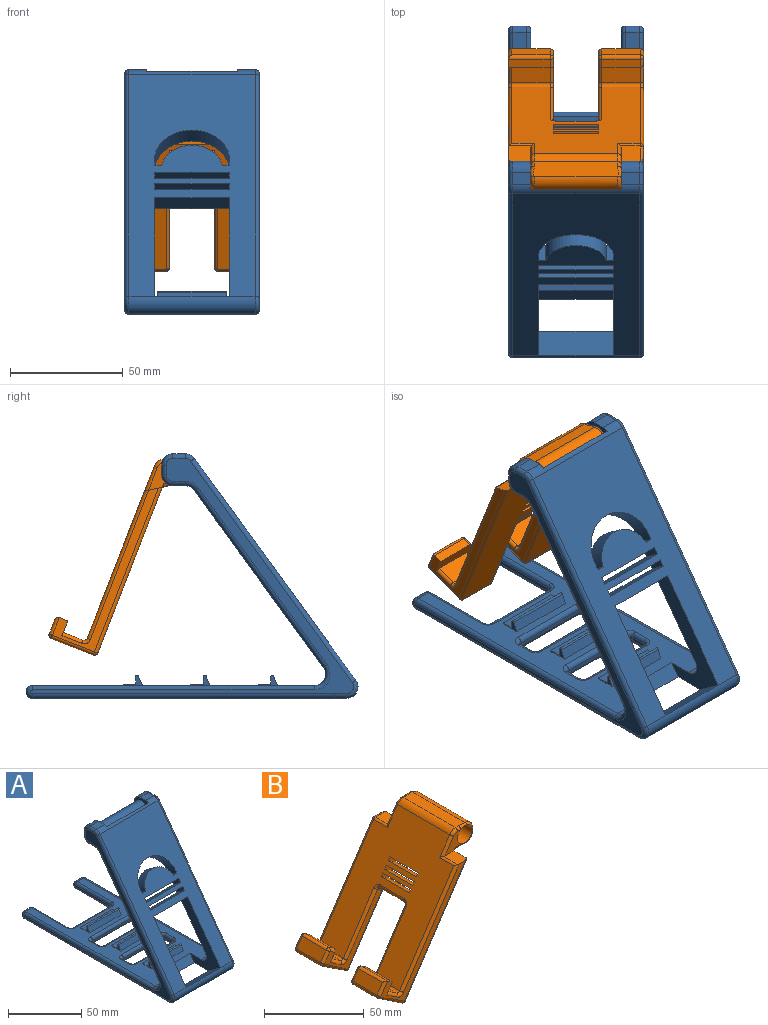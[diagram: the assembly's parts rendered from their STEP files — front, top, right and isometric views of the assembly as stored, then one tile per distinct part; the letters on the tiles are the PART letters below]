
ASSEMBLY  parts=2 mates=1
PART A: 162 faces, bbox 60x147.8x109.3 mm
  f0: plane 80.74x58.78mm, normal (0,0.81,-0.59), area 3689.6mm2, adj f2,f15,f18,f19,f20,f24,f26,f66
  f1: plane 98.49x71.71mm, normal (0,-0.81,0.59), area 4530.3mm2, adj f12,f23,f71,f130,f147,f148,f149,f150
  f2: cylinder r=5mm len=11.5mm, axis (-1,0,0), area 126.5mm2, adj f0,f3,f68,f148
  f3: plane 125.18x56mm, normal (0,0,1), area 2944.3mm2, adj f2,f5,f14,f15,f29,f33,f34,f35
  f4: plane 134.3x56mm, normal (0,0,-1), area 4121.6mm2, adj f5,f13,f14,f74,f81,f86,f87,f90
  f5: cylinder r=2.83mm len=6mm, axis (-1,0,0), area 53.3mm2, adj f3,f4,f122,f137
  f6: plane 8x4.2mm, normal (0,1,0), area 33.6mm2, adj f18,f22,f25,f138
  f7: plane 8x5.5mm, normal (0,0,1), area 44mm2, adj f18,f22,f23,f134
  f8: plane 8x5.5mm, normal (0,0,-1), area 44mm2, adj f20,f26,f27,f62
  f9: plane 8x5.5mm, normal (0,0,-1), area 44mm2, adj f18,f24,f25,f142
  f10: plane 8x4.2mm, normal (0,1,0), area 33.6mm2, adj f20,f27,f28,f63
  f11: plane 8x5.5mm, normal (0,0,1), area 44mm2, adj f20,f23,f28,f67
  f12: cylinder r=5mm len=56mm, axis (-1,0,0), area 613.6mm2, adj f1,f13,f73,f131,f145
  f13: plane 56x5.34mm, normal (0,-0.01,-1), area 299.3mm2, adj f4,f12,f75,f133
  f14: cylinder r=2.83mm len=6mm, axis (-1,0,0), area 53.3mm2, adj f3,f4,f72,f119
  f15: cylinder r=5mm len=11.5mm, axis (-1,0,0), area 126.5mm2, adj f0,f3,f141,f147
  f16: plane 143.43x104.54mm, normal (1,0,0), area 912.6mm2, adj f61,f62,f63,f64,f65,f66,f67,f68
  f17: plane 143.43x104.54mm, normal (-1,0,0), area 912.6mm2, adj f130,f131,f132,f133,f134,f135,f136,f137
  f18: plane 16.26x14.54mm, normal (1,0,0), area 96.4mm2, adj f0,f6,f7,f9,f19,f21,f22,f23
  f19: plane 40x13.51mm, normal (0,1,0), area 540.2mm2, adj f0,f18,f20,f23
  f20: plane 16.26x14.54mm, normal (-1,0,0), area 96.4mm2, adj f0,f8,f10,f11,f19,f21,f23,f26
  f21: cylinder r=5mm len=40mm, axis (-1,0,0), area 1256.6mm2, adj f18,f20
  f22: cylinder r=5mm len=8mm, axis (-1,0,0), area 62.8mm2, adj f6,f7,f18,f136
  f23: cylinder r=5mm len=56mm, axis (1,0,0), area 156.8mm2, adj f1,f7,f11,f18,f19,f20,f69,f132
  f24: cylinder r=5mm len=8mm, axis (-1,0,0), area 37.7mm2, adj f0,f9,f18,f144
  f25: cylinder r=5mm len=8mm, axis (-1,0,0), area 62.8mm2, adj f6,f9,f18,f140
  f26: cylinder r=5mm len=8mm, axis (-1,0,0), area 37.7mm2, adj f0,f8,f20,f64
  f27: cylinder r=5mm len=8mm, axis (-1,0,0), area 62.8mm2, adj f8,f10,f20,f61
  f28: cylinder r=5mm len=8mm, axis (-1,0,0), area 62.8mm2, adj f10,f11,f20,f65
  f29: plane 30.6x0.56mm, normal (0,1,0), area 17mm2, adj f3,f30,f34,f35
  f30: plane 30.6x5.48mm, normal (0,0,1), area 167.7mm2, adj f29,f31,f34,f35
  f31: plane 30.6x3.41mm, normal (0,1,0), area 104.3mm2, adj f30,f32,f34,f35
  f32: cylinder r=0.62mm len=30.6mm, axis (1,0,0), area 54.6mm2, adj f31,f33,f34,f35
  f33: plane 30.6x4.14mm, normal (0,-0.92,0.39), area 137.7mm2, adj f3,f32,f34,f35
  f34: plane 8.47x4.59mm, normal (-1,0,0), area 12.2mm2, adj f3,f29,f30,f31,f32,f33
  f35: plane 8.47x4.59mm, normal (1,0,0), area 12.2mm2, adj f3,f29,f30,f31,f32,f33
  f36: plane 30.6x0.56mm, normal (0,1,0), area 17mm2, adj f3,f37,f41,f42
  f37: plane 30.6x5.48mm, normal (0,0,1), area 167.7mm2, adj f36,f38,f41,f42
  f38: plane 30.6x3.41mm, normal (0,1,0), area 104.3mm2, adj f37,f39,f41,f42
  f39: cylinder r=0.62mm len=30.6mm, axis (1,0,0), area 54.6mm2, adj f38,f40,f41,f42
  f40: plane 30.6x4.14mm, normal (0,-0.92,0.39), area 137.7mm2, adj f3,f39,f41,f42
  f41: plane 8.47x4.59mm, normal (-1,0,0), area 12.2mm2, adj f3,f36,f37,f38,f39,f40
  f42: plane 8.47x4.59mm, normal (1,0,0), area 12.2mm2, adj f3,f36,f37,f38,f39,f40
  f43: plane 30.6x0.56mm, normal (0,1,0), area 17mm2, adj f3,f44,f48,f49
  f44: plane 30.6x5.48mm, normal (0,0,1), area 167.7mm2, adj f43,f45,f48,f49
  f45: plane 30.6x3.41mm, normal (0,1,0), area 104.3mm2, adj f44,f46,f48,f49
  f46: cylinder r=0.62mm len=30.6mm, axis (1,0,0), area 54.6mm2, adj f45,f47,f48,f49
  f47: plane 30.6x4.14mm, normal (0,-0.92,0.39), area 137.7mm2, adj f3,f46,f48,f49
  f48: plane 8.47x4.59mm, normal (-1,0,0), area 12.2mm2, adj f3,f43,f44,f45,f46,f47
  f49: plane 8.47x4.59mm, normal (1,0,0), area 12.2mm2, adj f3,f43,f44,f45,f46,f47
  f50: plane 36x1.65mm, normal (0,1,0), area 59.6mm2, adj f117,f124,f125,f129
  f51: plane 34.26x1.65mm, normal (-1,0,0), area 56.4mm2, adj f116,f119,f123,f124
  f52: plane 34.26x1.65mm, normal (1,0,0), area 56.4mm2, adj f118,f122,f125,f126
  f53: plane 36x1.65mm, normal (0,1,0), area 59.6mm2, adj f99,f100,f109,f110
  f54: plane 7x1.65mm, normal (-1,0,0), area 11.6mm2, adj f104,f109,f112,f115
  f55: plane 36x1.65mm, normal (0,-1,0), area 59.6mm2, adj f102,f103,f111,f112
  f56: plane 7x1.65mm, normal (1,0,0), area 11.6mm2, adj f96,f100,f101,f102
  f57: plane 36x1.65mm, normal (0,1,0), area 59.6mm2, adj f79,f80,f89,f90
  f58: plane 7x1.65mm, normal (-1,0,0), area 11.6mm2, adj f84,f89,f92,f95
  f59: plane 36x1.65mm, normal (0,-1,0), area 59.6mm2, adj f82,f83,f91,f92
  f60: plane 7x1.65mm, normal (1,0,0), area 11.6mm2, adj f76,f80,f81,f82
  f61: torus R=3mm, axis (1,0,0), area 21.1mm2, adj f16,f27,f62,f63
  f62: cylinder r=2mm len=5.5mm, axis (0,-1,0), area 17.3mm2, adj f8,f16,f61,f64
  f63: cylinder r=2mm len=4.2mm, axis (0,0,-1), area 13.2mm2, adj f10,f16,f61,f65
  f64: torus R=7mm, axis (1,0,0), area 16.9mm2, adj f16,f26,f62,f66
  f65: torus R=3mm, axis (1,0,0), area 21.1mm2, adj f16,f28,f63,f67
  f66: cylinder r=2mm len=79.86mm, axis (0,-0.59,-0.81), area 305.8mm2, adj f0,f16,f64,f68
  f67: cylinder r=2mm len=5.5mm, axis (0,1,0), area 17.3mm2, adj f11,f16,f65,f69
  f68: torus R=7mm, axis (1,0,0), area 39.6mm2, adj f2,f16,f66,f70
  f69: torus R=3mm, axis (1,0,0), area 12.6mm2, adj f16,f23,f67,f71
  f70: cylinder r=2mm len=125.18mm, axis (0,1,0), area 393.3mm2, adj f3,f16,f68,f72
  f71: cylinder r=2mm len=99.67mm, axis (0,0.59,0.81), area 382.7mm2, adj f1,f16,f69,f73
  f72: torus R=0.83mm, axis (1,0,0), area 20.7mm2, adj f14,f16,f70,f74
  f73: torus R=3mm, axis (1,0,0), area 29.4mm2, adj f12,f16,f71,f75
  f74: cylinder r=2mm len=134.3mm, axis (0,-1,0), area 421.9mm2, adj f4,f16,f72,f75
  f75: cylinder r=2mm len=5.36mm, axis (0,-1,0.01), area 16.8mm2, adj f13,f16,f73,f74
  f76: cylinder r=2mm len=7mm, axis (0,1,0), area 22mm2, adj f3,f60,f77,f78
  f77: torus R=4mm, axis (0,0,1), area 13.5mm2, adj f3,f76,f79,f80
  f78: torus R=4mm, axis (0,0,1), area 13.5mm2, adj f3,f76,f82,f83
  f79: cylinder r=2mm len=36mm, axis (-1,0,0), area 113.1mm2, adj f3,f57,f77,f85
  f80: cylinder r=2mm len=2mm, axis (0,0,-1), area 5.2mm2, adj f57,f60,f77,f86
  f81: cylinder r=2mm len=7mm, axis (0,-1,0), area 22mm2, adj f4,f60,f86,f87
  f82: cylinder r=2mm len=2mm, axis (0,0,1), area 5.2mm2, adj f59,f60,f78,f87
  f83: cylinder r=2mm len=36mm, axis (1,0,0), area 113.1mm2, adj f3,f59,f78,f88
  f84: cylinder r=2mm len=7mm, axis (0,-1,0), area 22mm2, adj f3,f58,f85,f88
  f85: torus R=4mm, axis (0,0,1), area 13.5mm2, adj f3,f79,f84,f89
  f86: torus R=4mm, axis (0,0,1), area 13.5mm2, adj f4,f80,f81,f90
  f87: torus R=4mm, axis (0,0,1), area 13.5mm2, adj f4,f81,f82,f91
  f88: torus R=4mm, axis (0,0,1), area 13.5mm2, adj f3,f83,f84,f92
  f89: cylinder r=2mm len=2mm, axis (0,0,1), area 5.2mm2, adj f57,f58,f85,f93
  f90: cylinder r=2mm len=36mm, axis (1,0,0), area 113.1mm2, adj f4,f57,f86,f93
  f91: cylinder r=2mm len=36mm, axis (-1,0,0), area 113.1mm2, adj f4,f59,f87,f94
  f92: cylinder r=2mm len=2mm, axis (0,0,-1), area 5.2mm2, adj f58,f59,f88,f94
  f93: torus R=4mm, axis (0,0,1), area 13.5mm2, adj f4,f89,f90,f95
  f94: torus R=4mm, axis (0,0,1), area 13.5mm2, adj f4,f91,f92,f95
  f95: cylinder r=2mm len=7mm, axis (0,1,0), area 22mm2, adj f4,f58,f93,f94
  f96: cylinder r=2mm len=7mm, axis (0,1,0), area 22mm2, adj f3,f56,f97,f98
  f97: torus R=4mm, axis (0,0,1), area 13.5mm2, adj f3,f96,f99,f100
  f98: torus R=4mm, axis (0,0,1), area 13.5mm2, adj f3,f96,f102,f103
  f99: cylinder r=2mm len=36mm, axis (-1,0,0), area 113.1mm2, adj f3,f53,f97,f105
  f100: cylinder r=2mm len=2mm, axis (0,0,-1), area 5.2mm2, adj f53,f56,f97,f106
  f101: cylinder r=2mm len=7mm, axis (0,-1,0), area 22mm2, adj f4,f56,f106,f107
  f102: cylinder r=2mm len=2mm, axis (0,0,1), area 5.2mm2, adj f55,f56,f98,f107
  f103: cylinder r=2mm len=36mm, axis (1,0,0), area 113.1mm2, adj f3,f55,f98,f108
  f104: cylinder r=2mm len=7mm, axis (0,-1,0), area 22mm2, adj f3,f54,f105,f108
  f105: torus R=4mm, axis (0,0,1), area 13.5mm2, adj f3,f99,f104,f109
  f106: torus R=4mm, axis (0,0,1), area 13.5mm2, adj f4,f100,f101,f110
  f107: torus R=4mm, axis (0,0,1), area 13.5mm2, adj f4,f101,f102,f111
  f108: torus R=4mm, axis (0,0,1), area 13.5mm2, adj f3,f103,f104,f112
  f109: cylinder r=2mm len=2mm, axis (0,0,1), area 5.2mm2, adj f53,f54,f105,f113
  f110: cylinder r=2mm len=36mm, axis (1,0,0), area 113.1mm2, adj f4,f53,f106,f113
  f111: cylinder r=2mm len=36mm, axis (-1,0,0), area 113.1mm2, adj f4,f55,f107,f114
  f112: cylinder r=2mm len=2mm, axis (0,0,-1), area 5.2mm2, adj f54,f55,f108,f114
  f113: torus R=4mm, axis (0,0,1), area 13.5mm2, adj f4,f109,f110,f115
  f114: torus R=4mm, axis (0,0,1), area 13.5mm2, adj f4,f111,f112,f115
  f115: cylinder r=2mm len=7mm, axis (0,1,0), area 22mm2, adj f4,f54,f113,f114
  f116: cylinder r=2mm len=33.44mm, axis (0,-1,0), area 105mm2, adj f3,f51,f119,f120
  f117: cylinder r=2mm len=36mm, axis (-1,0,0), area 113.1mm2, adj f3,f50,f120,f121
  f118: cylinder r=2mm len=33.44mm, axis (0,1,0), area 105mm2, adj f3,f52,f121,f122
  f119: torus R=0.83mm, axis (1,0,0), area 20.7mm2, adj f14,f51,f116,f123
  f120: torus R=4mm, axis (0,0,1), area 13.5mm2, adj f3,f116,f117,f124
  f121: torus R=4mm, axis (0,0,1), area 13.5mm2, adj f3,f117,f118,f125
  f122: torus R=0.83mm, axis (1,0,0), area 20.7mm2, adj f5,f52,f118,f126
  f123: cylinder r=2mm len=33.44mm, axis (0,1,0), area 105mm2, adj f4,f51,f119,f127
  f124: cylinder r=2mm len=2mm, axis (0,0,1), area 5.2mm2, adj f50,f51,f120,f127
  f125: cylinder r=2mm len=2mm, axis (0,0,-1), area 5.2mm2, adj f50,f52,f121,f128
  f126: cylinder r=2mm len=33.44mm, axis (0,-1,0), area 105mm2, adj f4,f52,f122,f128
  f127: torus R=4mm, axis (0,0,1), area 13.5mm2, adj f4,f123,f124,f129
  f128: torus R=4mm, axis (0,0,1), area 13.5mm2, adj f4,f125,f126,f129
  f129: cylinder r=2mm len=36mm, axis (1,0,0), area 113.1mm2, adj f4,f50,f127,f128
  f130: cylinder r=2mm len=99.67mm, axis (0,-0.59,-0.81), area 382.7mm2, adj f1,f17,f131,f132
  f131: torus R=3mm, axis (1,0,0), area 29.4mm2, adj f12,f17,f130,f133
  f132: torus R=3mm, axis (1,0,0), area 12.6mm2, adj f17,f23,f130,f134
  f133: cylinder r=2mm len=5.36mm, axis (0,1,-0.01), area 16.8mm2, adj f13,f17,f131,f135
  f134: cylinder r=2mm len=5.5mm, axis (0,-1,0), area 17.3mm2, adj f7,f17,f132,f136
  f135: cylinder r=2mm len=134.3mm, axis (0,1,0), area 421.9mm2, adj f4,f17,f133,f137
  f136: torus R=3mm, axis (1,0,0), area 21.1mm2, adj f17,f22,f134,f138
  f137: torus R=0.83mm, axis (1,0,0), area 20.7mm2, adj f5,f17,f135,f139
  f138: cylinder r=2mm len=4.2mm, axis (0,0,1), area 13.2mm2, adj f6,f17,f136,f140
  f139: cylinder r=2mm len=125.18mm, axis (0,-1,0), area 393.3mm2, adj f3,f17,f137,f141
  f140: torus R=3mm, axis (1,0,0), area 21.1mm2, adj f17,f25,f138,f142
  f141: torus R=7mm, axis (1,0,0), area 39.6mm2, adj f15,f17,f139,f143
  f142: cylinder r=2mm len=5.5mm, axis (0,1,0), area 17.3mm2, adj f9,f17,f140,f144
  f143: cylinder r=2mm len=79.86mm, axis (0,0.59,0.81), area 305.8mm2, adj f0,f17,f141,f144
  f144: torus R=7mm, axis (1,0,0), area 16.9mm2, adj f17,f24,f142,f143
  f145: plane 33x10.97mm, normal (0,0.59,0.81), area 448mm2, adj f4,f12,f147,f148
  f146: plane 33x5.65mm, normal (0,-0.81,0.59), area 230.8mm2, adj f3,f4,f147,f148
  f147: plane 51.67x38.56mm, normal (1,0,0), area 579.7mm2, adj f0,f1,f3,f4,f15,f145,f146,f149
  f148: plane 51.67x38.56mm, normal (-1,0,0), area 579.7mm2, adj f0,f1,f2,f3,f4,f145,f146,f149
  f149: plane 33x6.76mm, normal (0,-0.59,-0.81), area 275.8mm2, adj f0,f1,f147,f148
  f150: cylinder r=16.72mm len=33.45mm, axis (0,-0.81,0.59), area 484.9mm2, adj f0,f1,f151,f153
  f151: plane 6.76x4.92mm, normal (0,0.59,0.81), area 25.3mm2, adj f0,f1,f150,f152
  f152: cylinder r=13.71mm len=26.95mm, axis (0,-0.81,0.59), area 317.6mm2, adj f0,f1,f151,f153
  f153: plane 6.76x4.92mm, normal (0,0.59,0.81), area 25.3mm2, adj f0,f1,f150,f152
  f154: plane 33x6.76mm, normal (0,-0.59,-0.81), area 275.8mm2, adj f0,f1,f155,f157
  f155: plane 8.67x7.54mm, normal (1,0,0), area 27.1mm2, adj f0,f1,f154,f156
  f156: plane 33x6.76mm, normal (0,0.59,0.81), area 275.8mm2, adj f0,f1,f155,f157
  f157: plane 8.67x7.54mm, normal (-1,0,0), area 27.1mm2, adj f0,f1,f154,f156
  f158: plane 33x6.76mm, normal (0,-0.59,-0.81), area 275.8mm2, adj f0,f1,f159,f161
  f159: plane 8.52x7.34mm, normal (1,0,0), area 25mm2, adj f0,f1,f158,f160
  f160: plane 33x6.76mm, normal (0,0.59,0.81), area 275.8mm2, adj f0,f1,f159,f161
  f161: plane 8.52x7.34mm, normal (-1,0,0), area 25mm2, adj f0,f1,f158,f160
PART B: 119 faces, bbox 78.2x60.4x79.3 mm
  f0: plane 68.21x57mm, normal (-0.83,0,0.55), area 3330mm2, adj f10,f30,f53,f56,f60,f63,f65,f66
  f1: plane 17x16.73mm, normal (-0.55,0,-0.83), area 341.7mm2, adj f7,f8,f35,f99
  f2: plane 67.66x57.42mm, normal (0.83,0,-0.55), area 3313.9mm2, adj f8,f11,f12,f13,f24,f26,f31,f36
  f3: plane 17x7.79mm, normal (0.55,0,0.83), area 159.2mm2, adj f4,f10,f62,f93
  f4: plane 20x5.9mm, normal (0.83,0,-0.55), area 112.4mm2, adj f3,f5,f21,f62,f77,f91,f93
  f5: plane 18.5x3.35mm, normal (0.55,0,0.83), area 74.5mm2, adj f4,f9,f21,f91
  f6: plane 17x5.85mm, normal (-0.83,0,0.55), area 119.5mm2, adj f7,f9,f42,f94
  f7: cylinder r=1.5mm len=17mm, axis (0,1,0), area 40.1mm2, adj f1,f6,f38,f96
  f8: cylinder r=1.5mm len=17mm, axis (0,-1,0), area 40.1mm2, adj f1,f2,f40,f102
  f9: cylinder r=1.5mm len=18.5mm, axis (0,1,0), area 41.8mm2, adj f5,f6,f42,f92
  f10: cylinder r=1.5mm len=17mm, axis (0,1,0), area 40.1mm2, adj f0,f3,f64,f95
  f11: plane 11.78x10.6mm, normal (0,1,0), area 59mm2, adj f2,f26,f27,f31,f46,f50,f53
  f12: plane 11.78x10.6mm, normal (0,-1,0), area 59mm2, adj f2,f24,f27,f67,f68,f69,f75
  f13: plane 37x9.2mm, normal (0,0,-1), area 340.5mm2, adj f2,f28,f31,f75
  f14: plane 37.07x2.1mm, normal (1,0,0), area 77.7mm2, adj f28,f29,f34,f72
  f15: plane 37.61x6.53mm, normal (0,0,1), area 243.1mm2, adj f29,f30,f41,f46,f69,f70
  f16: plane 17x16.73mm, normal (-0.55,0,-0.83), area 341.7mm2, adj f39,f44,f45,f114
  f17: plane 17x7.79mm, normal (0.55,0,0.83), area 159.2mm2, adj f18,f59,f63,f97
  f18: plane 18.5x5.9mm, normal (0.83,0,-0.55), area 103.5mm2, adj f17,f19,f57,f78,f97,f118
  f19: plane 17x3.35mm, normal (0.55,0,0.83), area 68.5mm2, adj f18,f47,f54,f118
  f20: plane 17x5.85mm, normal (-0.83,0,0.55), area 119.5mm2, adj f39,f47,f48,f116
  f21: plane 64.91x60mm, normal (0,-1,0), area 338.9mm2, adj f4,f5,f24,f35,f36,f42,f62,f64
  f22: plane 63.41x59mm, normal (0,1,0), area 317.7mm2, adj f44,f48,f52,f54,f55,f57,f59,f60
  f23: plane 2.49x2.17mm, normal (0,-1,0), area 0.3mm2, adj f27,f74
  f24: plane 10.67x7.68mm, normal (0,0,1), area 72mm2, adj f2,f12,f21,f36,f65,f66,f67
  f25: plane 2.49x2.17mm, normal (0,1,0), area 0.3mm2, adj f27,f32
  f26: plane 8.78x7.29mm, normal (0,0,1), area 61.8mm2, adj f2,f11,f53,f55,f56
  f27: cylinder r=5.26mm len=40mm, axis (0,-1,0), area 1320.7mm2, adj f11,f12,f23,f25,f31,f32,f33,f34
  f28: cylinder r=5mm len=37.02mm, axis (0,1,0), area 290.6mm2, adj f13,f14,f32,f33,f73,f74
  f29: cylinder r=5mm len=37.32mm, axis (0,1,0), area 292mm2, adj f14,f15,f37,f71
  f30: cylinder r=5mm len=37mm, axis (0,1,0), area 181.8mm2, adj f0,f15,f50,f68
  f31: cylinder r=1.5mm len=9.2mm, axis (1,0,0), area 19.1mm2, adj f2,f11,f13,f27,f32
  f32: torus R=3.5mm, axis (0,-1,0), area 13.9mm2, adj f25,f27,f28,f31,f33
  f33: bspline ~1.59x1.5mm, area 2.3mm2, adj f27,f28,f32,f34
  f34: bspline ~3.72x1.62mm, area 4.5mm2, adj f14,f27,f33,f37
  f35: cylinder r=1.5mm len=17.56mm, axis (-0.83,0,0.55), area 47.4mm2, adj f1,f21,f38,f40
  f36: cylinder r=1.5mm len=66.58mm, axis (-0.55,0,-0.83), area 185mm2, adj f2,f21,f24,f40
  f37: bspline ~5x5mm, area 14.8mm2, adj f27,f29,f34,f41
  f38: sphere r=1.5mm, area 3.2mm2, adj f7,f35,f42
  f39: cylinder r=1.5mm len=17mm, axis (0,1,0), area 40.1mm2, adj f16,f20,f43,f115
  f40: sphere r=1.5mm, area 3.5mm2, adj f8,f35,f36
  f41: bspline ~5.64x1.79mm, area 7.4mm2, adj f15,f27,f37,f46
  f42: cylinder r=1.5mm len=7.93mm, axis (0.55,0,0.83), area 18.3mm2, adj f6,f9,f21,f38
  f43: sphere r=1.5mm, area 3.2mm2, adj f39,f44,f48
  f44: cylinder r=1.5mm len=17.56mm, axis (0.83,0,-0.55), area 47.4mm2, adj f16,f22,f43,f49
  f45: cylinder r=1.5mm len=17mm, axis (0,-1,0), area 40.1mm2, adj f2,f16,f49,f113
  f46: cylinder r=1.5mm len=2.14mm, axis (1,0,0), area 5mm2, adj f11,f15,f41,f50
  f47: cylinder r=1.5mm len=17mm, axis (0,1,0), area 40.1mm2, adj f19,f20,f51,f117
  f48: cylinder r=1.5mm len=6.68mm, axis (-0.55,0,-0.83), area 16.6mm2, adj f20,f22,f43,f51
  f49: sphere r=1.5mm, area 3.3mm2, adj f44,f45,f52
  f50: torus R=3.5mm, axis (0,-1,0), area 10.3mm2, adj f11,f30,f46,f53
  f51: sphere r=1.5mm, area 3.8mm2, adj f47,f48,f54
  f52: cylinder r=1.5mm len=66.58mm, axis (0.55,0,0.83), area 183.8mm2, adj f2,f22,f49,f55
  f53: cylinder r=1.5mm len=11.37mm, axis (-0.55,0,-0.83), area 27.6mm2, adj f0,f11,f26,f50,f56
  f54: cylinder r=1.5mm len=4.18mm, axis (-0.83,0,0.55), area 7.7mm2, adj f19,f22,f51,f57
  f55: cylinder r=1.5mm len=7.26mm, axis (1,0,0), area 14.7mm2, adj f22,f26,f52,f58
  f56: cylinder r=1.5mm len=10mm, axis (0,1,0), area 13.8mm2, adj f0,f26,f53,f58
  f57: cylinder r=1.5mm len=6.74mm, axis (0.55,0,0.83), area 13.2mm2, adj f18,f22,f54,f59
  f58: sphere r=1.5mm, area 2.5mm2, adj f55,f56,f60
  f59: cylinder r=1.5mm len=9.87mm, axis (-0.83,0,0.55), area 23.8mm2, adj f17,f22,f57,f61
  f60: cylinder r=1.5mm len=58.5mm, axis (-0.55,0,-0.83), area 163.3mm2, adj f0,f22,f58,f61
  f61: torus R=3mm, axis (0,-1,0), area 7.6mm2, adj f22,f59,f60,f63
  f62: cylinder r=1.5mm len=8.62mm, axis (0.83,0,-0.55), area 22.1mm2, adj f3,f4,f21,f64
  f63: cylinder r=1.5mm len=17mm, axis (0,1,0), area 40.1mm2, adj f0,f17,f61,f100
  f64: torus R=3mm, axis (0,-1,0), area 7.6mm2, adj f10,f21,f62,f65
  f65: cylinder r=1.5mm len=60mm, axis (0.55,0,0.83), area 165.6mm2, adj f0,f21,f24,f64,f66
  f66: cylinder r=1.5mm len=11.25mm, axis (0,1,0), area 14.7mm2, adj f0,f24,f65,f67
  f67: cylinder r=1.5mm len=11.37mm, axis (0.55,0,0.83), area 27.6mm2, adj f0,f12,f24,f66,f68
  f68: torus R=3.5mm, axis (0,-1,0), area 10.3mm2, adj f12,f30,f67,f69
  f69: cylinder r=1.5mm len=2.14mm, axis (-1,0,0), area 5mm2, adj f12,f15,f68,f70
  f70: bspline ~5.64x1.79mm, area 7.4mm2, adj f15,f27,f69,f71
  f71: bspline ~5x5mm, area 14.8mm2, adj f27,f29,f70,f72
  f72: bspline ~3.72x1.62mm, area 4.5mm2, adj f14,f27,f71,f73
  f73: bspline ~1.59x1.5mm, area 2.3mm2, adj f27,f28,f72,f74
  f74: torus R=3.5mm, axis (0,-1,0), area 13.9mm2, adj f23,f27,f28,f73,f75
  f75: cylinder r=1.5mm len=9.2mm, axis (-1,0,0), area 19.1mm2, adj f2,f12,f13,f27,f74
  f76: plane 17x3.09mm, normal (-0.55,0,-0.83), area 63.1mm2, adj f104,f105,f109,f110
  f77: plane 40.8x38.17mm, normal (0,1,0), area 209mm2, adj f4,f91,f93,f94,f95,f98,f99,f105
  f78: plane 40.8x38.17mm, normal (0,-1,0), area 209mm2, adj f18,f97,f100,f103,f109,f112,f114,f116
  f79: plane 6.81x5.57mm, normal (0,-1,0), area 14.9mm2, adj f0,f2,f80,f82
  f80: plane 20x5.58mm, normal (0.55,0,0.83), area 134.2mm2, adj f0,f2,f79,f81
  f81: plane 6.81x5.57mm, normal (0,1,0), area 14.9mm2, adj f0,f2,f80,f82
  f82: plane 20x5.58mm, normal (-0.55,0,-0.83), area 134.2mm2, adj f0,f2,f79,f81
  f83: plane 6.74x5.46mm, normal (0,-1,0), area 14mm2, adj f0,f2,f84,f86
  f84: plane 20x5.58mm, normal (0.55,0,0.83), area 134.2mm2, adj f0,f2,f83,f85
  f85: plane 6.74x5.46mm, normal (0,1,0), area 14mm2, adj f0,f2,f84,f86
  f86: plane 20x5.58mm, normal (-0.55,0,-0.83), area 134.2mm2, adj f0,f2,f83,f85
  f87: plane 20x5.58mm, normal (0.55,0,0.83), area 134.2mm2, adj f0,f2,f88,f90
  f88: plane 6.74x5.46mm, normal (0,1,0), area 14mm2, adj f0,f2,f87,f89
  f89: plane 20x5.58mm, normal (-0.55,0,-0.83), area 134.2mm2, adj f0,f2,f88,f90
  f90: plane 6.74x5.46mm, normal (0,-1,0), area 14mm2, adj f0,f2,f87,f89
  f91: cylinder r=1.5mm len=4.18mm, axis (-0.83,0,0.55), area 9.5mm2, adj f4,f5,f77,f92
  f92: sphere r=1.5mm, area 3.5mm2, adj f9,f91,f94
  f93: cylinder r=1.5mm len=8.62mm, axis (-0.83,0,0.55), area 22.1mm2, adj f3,f4,f77,f95
  f94: cylinder r=1.5mm len=6.68mm, axis (-0.55,0,-0.83), area 16.6mm2, adj f6,f77,f92,f96
  f95: torus R=3mm, axis (0,1,0), area 7.6mm2, adj f10,f77,f93,f98
  f96: sphere r=1.5mm, area 3.5mm2, adj f7,f94,f99
  f97: cylinder r=1.5mm len=8.62mm, axis (0.83,0,-0.55), area 22.1mm2, adj f17,f18,f78,f100
  f98: cylinder r=1.5mm len=33.26mm, axis (-0.55,0,-0.83), area 91.8mm2, adj f0,f77,f95,f101
  f99: cylinder r=1.5mm len=17.56mm, axis (0.83,0,-0.55), area 47.4mm2, adj f1,f77,f96,f102
  f100: torus R=3mm, axis (0,1,0), area 7.6mm2, adj f63,f78,f97,f103
  f101: torus R=3mm, axis (0.83,0,-0.55), area 7.6mm2, adj f0,f98,f104,f105
  f102: sphere r=1.5mm, area 3.1mm2, adj f8,f99,f106
  f103: cylinder r=1.5mm len=33.26mm, axis (0.55,0,0.83), area 91.8mm2, adj f0,f78,f100,f107
  f104: cylinder r=1.5mm len=17mm, axis (0,-1,0), area 40.1mm2, adj f0,f76,f101,f107
  f105: cylinder r=1.5mm len=3.92mm, axis (0.83,0,-0.55), area 8.7mm2, adj f76,f77,f101,f108
  f106: cylinder r=1.5mm len=36.95mm, axis (0.55,0,0.83), area 102.3mm2, adj f2,f77,f102,f108
  f107: torus R=3mm, axis (0.83,0,-0.55), area 7.6mm2, adj f0,f103,f104,f109
  f108: torus R=3mm, axis (-0.83,0,0.55), area 7.6mm2, adj f2,f105,f106,f110
  f109: cylinder r=1.5mm len=3.92mm, axis (-0.83,0,0.55), area 8.7mm2, adj f76,f78,f107,f111
  f110: cylinder r=1.5mm len=17mm, axis (0,1,0), area 40.1mm2, adj f2,f76,f108,f111
  f111: torus R=3mm, axis (-0.83,0,0.55), area 7.6mm2, adj f2,f109,f110,f112
  f112: cylinder r=1.5mm len=36.95mm, axis (-0.55,0,-0.83), area 102.3mm2, adj f2,f78,f111,f113
  f113: sphere r=1.5mm, area 3.5mm2, adj f45,f112,f114
  f114: cylinder r=1.5mm len=17.56mm, axis (-0.83,0,0.55), area 47.4mm2, adj f16,f78,f113,f115
  f115: sphere r=1.5mm, area 4mm2, adj f39,f114,f116
  f116: cylinder r=1.5mm len=6.68mm, axis (0.55,0,0.83), area 16.6mm2, adj f20,f78,f115,f117
  f117: sphere r=1.5mm, area 3.1mm2, adj f47,f116,f118
  f118: cylinder r=1.5mm len=4.18mm, axis (0.83,0,-0.55), area 9.5mm2, adj f18,f19,f78,f117
PLACE A t=(-90.92,-44.62,139.6)mm
PLACE B rot(axis=(-0.11,-0.11,-0.99),90.7deg) t=(-60.92,-38.98,133.1)mm
MATE revolute B.f27 <-> A.f21  axis (-1,0,0) through (-70.92,-38.1,194.15)mm
